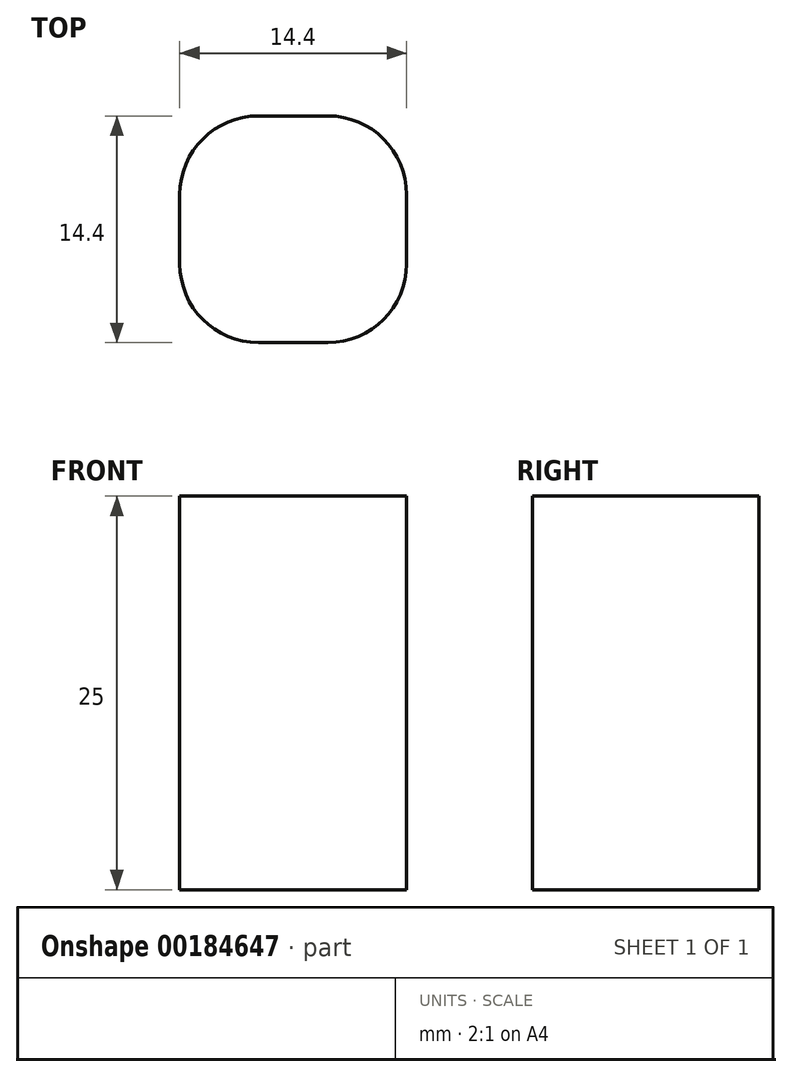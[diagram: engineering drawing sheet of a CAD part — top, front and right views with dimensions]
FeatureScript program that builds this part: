
annotation { "Feature Type Name" : "Feature", "Feature Type Description" : "" }
export const myFeature = defineFeature(function(context is Context, id is Id, definition is map)
    precondition{}
    {
        {
            var Q0;
            Q0=qCreatedBy(makeId("Top.planeOp"),FACE);
            var sketch = newSketch(context, id + "F0", { "sketchPlane" : qUnion([Q0])});
            skLineSegment(sketch, "E0.bottom", {"start": v(2.2, 7.2) * mm, "end": v(-2.2, 7.2) * mm});
            skLineSegment(sketch, "E0.top", {"start": v(2.2, -7.2) * mm, "end": v(-2.2, -7.2) * mm});
            skLineSegment(sketch, "E0.left", {"start": v(7.2, 2.2) * mm, "end": v(7.2, -2.2) * mm});
            skLineSegment(sketch, "E0.right", {"start": v(-7.2, 2.2) * mm, "end": v(-7.2, -2.2) * mm});
            skPoint(sketch, "E0.middle", {"position": v(0, 0) * mm});
            skPoint(sketch, "E1.visualSharp", {"position": v(-7.2, 7.2) * mm});
            skArc(sketch, "E1.filletArc", {"start": v(-2.2, 7.2) * mm, "mid": v(-5.74, 5.74) * mm, "end": v(-7.2, 2.2) * mm});
            skPoint(sketch, "E2.visualSharp", {"position": v(7.2, 7.2) * mm});
            skArc(sketch, "E2.filletArc", {"start": v(7.2, 2.2) * mm, "mid": v(5.74, 5.74) * mm, "end": v(2.2, 7.2) * mm});
            skPoint(sketch, "E3.visualSharp", {"position": v(7.2, -7.2) * mm});
            skArc(sketch, "E3.filletArc", {"start": v(2.2, -7.2) * mm, "mid": v(5.74, -5.74) * mm, "end": v(7.2, -2.2) * mm});
            skPoint(sketch, "E4.visualSharp", {"position": v(-7.2, -7.2) * mm});
            skArc(sketch, "E4.filletArc", {"start": v(-7.2, -2.2) * mm, "mid": v(-5.74, -5.74) * mm, "end": v(-2.2, -7.2) * mm});
            skSolve(sketch);
        }
        {
            var Q0;
            Q0 = qSketchRegion(id + "F0", true);
            extrude(context, id + "F1", {"entities" : qUnion([Q0]), "depth" : 25 * mm, "offsetDistance" : 25 * mm});
        }
    });
